# Revit family: ledflood-e2_re113-10w-3000-bl_543017020400
name_source: partatom
category: Leuchten
revit_build: Autodesk Revit 2016 (Build: 20190508_0715(x64)
units: mm (PartAtom-declared; Revit-internal decimal feet)

## family parameters
Basisbauteil = Fläche
Beim Laden mit Abzugskörper schneiden = Nein
Bemaßung runder Anschluss = Durchmesser verwenden
Gemeinsam genutzt = Nein
Lichtquelle = Nein
Raumberechnungspunkt = Nein
Teiletyp = Normal

## types (1)
- LEDFlood-E2 Re113-10W-3000-BL (1 x LED, 1050 lm)
    Approval mark = CE
    Beschreibung = Compact aluminium design with clipless cover. IP66 protection level against water and dust. High energy saving compared to halogen and high pressure sodium lamps. Compatible brackets and ground spikes available. IP65 daylight and motion sensor accessory available.
    CIE Flux Codes = 52 83 97 100 100
    Control Gear = Electronic ballast
    Height = 844 mm
    Hersteller = OPPLE
    Lamp Light Flux = 1050 lm
    Lamp count = 1
    Lampe = 1 x LED
    Length = 104 mm  [stored 0.341207 ft]
    Luminous efficacy = 105 lm/W
    ModVariant = Nein
    Modell = 543017020400
    Mounting Place = Wall
    Mounting Type = Surface mounted
    Number of Poles = 1
    OnlyDefault = Ja
    Power Factor = 1
    Product Name = LEDFlood-E2 Re113-10W-3000-BL
    Product group = Floodlight EcoMax G2 Low Power
    ProductGroupID = 2003
    Protection Class = Protection class I
    Protection Degree = IP 66
    RLX_Detail_Level = 1
    RlxData = <blob elided: 110369 chars, md5=d98334e0>
    Scheinlast = 10 VA
    Socket = socket
    Standby Power = 0 W
    System Light Flux = 1050 lm
    System Power = 10 W
    Typenbild = 543017020400.jpg
    Typenkommentare = Product without accessories
    URL = http://relux.com
    VarID = ---
    Voltage = 0 V
    Vorgabe-Ansicht = 1800 mm
    Weight = 0.00 kg
    Width = 113 mm

note: [stored X ft] marks values corroborated as IEEE doubles in the binary element streams (Revit-internal decimal feet)

## geometry (parser evidence)
native form markers: Sweep x12
no freeform markers — native parametric forms only
